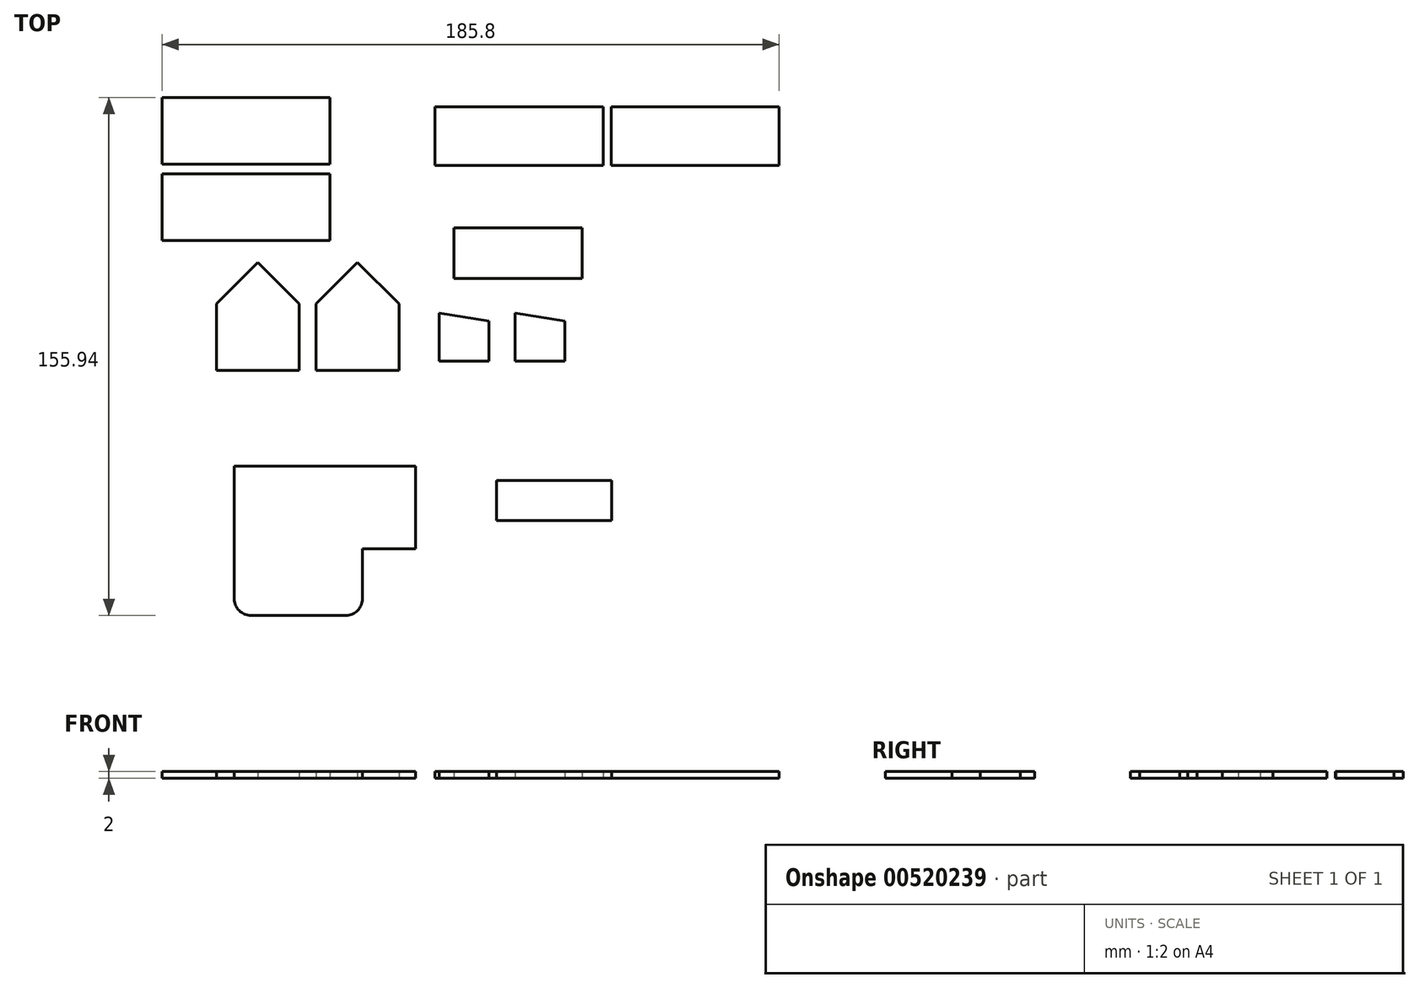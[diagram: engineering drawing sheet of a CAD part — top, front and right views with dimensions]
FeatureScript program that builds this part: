
annotation { "Feature Type Name" : "Feature", "Feature Type Description" : "" }
export const myFeature = defineFeature(function(context is Context, id is Id, definition is map)
    precondition{}
    {
        {
            var Q0;
            Q0=qCreatedBy(makeId("Top.planeOp"),FACE);
            var sketch = newSketch(context, id + "F0", { "sketchPlane" : qUnion([Q0])});
            skLineSegment(sketch, "E0.bottom", {"start": v(-52.9, 38.15) * mm, "end": v(-27.9, 38.15) * mm});
            skLineSegment(sketch, "E0.top", {"start": v(-52.9, 18.15) * mm, "end": v(-27.9, 18.15) * mm});
            skLineSegment(sketch, "E0.left", {"start": v(-52.9, 38.15) * mm, "end": v(-52.9, 18.15) * mm});
            skLineSegment(sketch, "E0.right", {"start": v(-27.9, 38.15) * mm, "end": v(-27.9, 18.15) * mm});
            skLineSegment(sketch, "E1", {"start": v(-52.9, 38.15) * mm, "end": v(-40.4, 50.65) * mm});
            skLineSegment(sketch, "E2", {"start": v(-40.4, 50.65) * mm, "end": v(-27.9, 38.15) * mm});
            skSolve(sketch);
        }
        {
            var Q0;
            Q0 = qSketchRegion(id + "F0", true);
            extrude(context, id + "F1", {"entities" : qUnion([Q0]), "depth" : 2 * mm, "offsetDistance" : 25 * mm});
        }
        {
            var Q0;
            Q0=makeQuery(id+"F1.opExtrude","SWEPT_BODY",BODY,{"disambiguationData":[OSD([sQuery(id+"F0.wireOp",EDGE,"E0.top"),sQuery(id+"F0.wireOp",EDGE,"E0.left"),sQuery(id+"F0.wireOp",EDGE,"E0.right"),sQuery(id+"F0.wireOp",EDGE,"E1"),sQuery(id+"F0.wireOp",EDGE,"E2")])]});
            transform(context, id + "F2", {"entities" : qUnion([Q0]), "transformType" : TransformType.TRANSLATION_3D, "dx" : 30 * mm, "dy" : 0 * mm, "dz" : 0 * mm, "makeCopy" : true});
        }
        {
            var Q0;
            Q0=qCreatedBy(makeId("Top.planeOp"),FACE);
            var sketch = newSketch(context, id + "F3", { "sketchPlane" : qUnion([Q0])});
            skLineSegment(sketch, "E3.bottom", {"start": v(-47.49, -10.67) * mm, "end": v(7.1, -10.67) * mm});
            skLineSegment(sketch, "E3.top", {"start": v(-47.49, -35.67) * mm, "end": v(7.1, -35.67) * mm});
            skLineSegment(sketch, "E3.left", {"start": v(-47.49, -10.67) * mm, "end": v(-47.49, -35.67) * mm});
            skLineSegment(sketch, "E3.right", {"start": v(7.1, -10.67) * mm, "end": v(7.1, -35.67) * mm});
            skLineSegment(sketch, "E4.bottom", {"start": v(-47.49, -35.67) * mm, "end": v(-8.87, -35.67) * mm});
            skLineSegment(sketch, "E4.top", {"start": v(-42.49, -55.67) * mm, "end": v(-13.87, -55.67) * mm});
            skLineSegment(sketch, "E4.left", {"start": v(-47.49, -35.67) * mm, "end": v(-47.49, -50.67) * mm});
            skLineSegment(sketch, "E4.right", {"start": v(-8.87, -35.67) * mm, "end": v(-8.87, -50.67) * mm});
            skPoint(sketch, "E5.visualSharp", {"position": v(-47.49, -55.67) * mm});
            skArc(sketch, "E5.filletArc", {"start": v(-47.49, -50.67) * mm, "mid": v(-46.02, -54.2) * mm, "end": v(-42.49, -55.67) * mm});
            skPoint(sketch, "E6.visualSharp", {"position": v(-8.87, -55.67) * mm});
            skArc(sketch, "E6.filletArc", {"start": v(-13.87, -55.67) * mm, "mid": v(-10.34, -54.2) * mm, "end": v(-8.87, -50.67) * mm});
            skSolve(sketch);
        }
        {
            var Q0;
            Q0 = qSketchRegion(id + "F3", true);
            extrude(context, id + "F4", {"entities" : qUnion([Q0]), "depth" : 2 * mm, "offsetDistance" : 25 * mm});
        }
        {
            var Q0;
            Q0=qCreatedBy(makeId("Top.planeOp"),FACE);
            var sketch = newSketch(context, id + "F5", { "sketchPlane" : qUnion([Q0])});
            skLineSegment(sketch, "E7.bottom", {"start": v(37.04, 32.92) * mm, "end": v(52.04, 32.92) * mm});
            skLineSegment(sketch, "E7.top", {"start": v(37.04, 20.92) * mm, "end": v(52.04, 20.92) * mm});
            skLineSegment(sketch, "E7.left", {"start": v(37.04, 32.92) * mm, "end": v(37.04, 20.92) * mm});
            skLineSegment(sketch, "E7.right", {"start": v(52.04, 32.92) * mm, "end": v(52.04, 20.92) * mm});
            skLineSegment(sketch, "E8", {"start": v(37.04, 32.92) * mm, "end": v(37.04, 35.42) * mm});
            skLineSegment(sketch, "E9", {"start": v(37.04, 35.42) * mm, "end": v(52.04, 32.92) * mm});
            skSolve(sketch);
        }
        {
            var Q0;
            Q0 = qSketchRegion(id + "F5", true);
            extrude(context, id + "F6", {"entities" : qUnion([Q0]), "depth" : 2 * mm, "offsetDistance" : 25 * mm});
        }
        {
            var Q0;
            Q0=makeQuery(id+"F6.opExtrude","SWEPT_BODY",BODY,{"disambiguationData":[OSD([sQuery(id+"F5.wireOp",EDGE,"E7.top"),sQuery(id+"F5.wireOp",EDGE,"E7.left"),sQuery(id+"F5.wireOp",EDGE,"E7.right"),sQuery(id+"F5.wireOp",EDGE,"E8"),sQuery(id+"F5.wireOp",EDGE,"E9")])]});
            transform(context, id + "F7", {"entities" : qUnion([Q0]), "transformType" : TransformType.TRANSLATION_3D, "dx" : -22.8 * mm, "dy" : 0 * mm, "dz" : 0 * mm, "makeCopy" : true});
        }
        {
            var Q0;
            Q0=qCreatedBy(makeId("Top.planeOp"),FACE);
            var sketch = newSketch(context, id + "F8", { "sketchPlane" : qUnion([Q0])});
            skLineSegment(sketch, "E10.bottom", {"start": v(31.5, -15.05) * mm, "end": v(66.1, -15.05) * mm});
            skLineSegment(sketch, "E10.top", {"start": v(31.5, -27.05) * mm, "end": v(66.1, -27.05) * mm});
            skLineSegment(sketch, "E10.left", {"start": v(31.5, -15.05) * mm, "end": v(31.5, -27.05) * mm});
            skLineSegment(sketch, "E10.right", {"start": v(66.1, -15.05) * mm, "end": v(66.1, -27.05) * mm});
            skSolve(sketch);
        }
        {
            var Q0;
            Q0=makeQuery(id+"F8.imprint","IMPRINT",FACE,{"disambiguationData":[TD([[makeQuery(id+"F8.imprint","IMPRINT",EDGE,{"derivedFrom":sQuery(id+"F8.wireOp",EDGE,"E10.bottom")}),-1.0]])]});
            extrude(context, id + "F9", {"entities" : qUnion([Q0]), "depth" : 2 * mm, "offsetDistance" : 25 * mm});
        }
        {
            var Q0;
            Q0=qCreatedBy(makeId("Top.planeOp"),FACE);
            var sketch = newSketch(context, id + "F10", { "sketchPlane" : qUnion([Q0])});
            skLineSegment(sketch, "E11.bottom", {"start": v(18.6, 61.06) * mm, "end": v(57.22, 61.06) * mm});
            skLineSegment(sketch, "E11.top", {"start": v(18.6, 45.85) * mm, "end": v(57.22, 45.85) * mm});
            skLineSegment(sketch, "E11.left", {"start": v(18.6, 61.06) * mm, "end": v(18.6, 45.85) * mm});
            skLineSegment(sketch, "E11.right", {"start": v(57.22, 61.06) * mm, "end": v(57.22, 45.85) * mm});
            skSolve(sketch);
        }
        {
            var Q0;
            Q0 = qSketchRegion(id + "F10", true);
            extrude(context, id + "F11", {"entities" : qUnion([Q0]), "depth" : 2 * mm, "offsetDistance" : 25 * mm});
        }
        {
            var Q0;
            Q0=qCreatedBy(makeId("Top.planeOp"),FACE);
            var sketch = newSketch(context, id + "F12", { "sketchPlane" : qUnion([Q0])});
            skLineSegment(sketch, "E12.bottom", {"start": v(-69.22, 77.27) * mm, "end": v(-18.63, 77.27) * mm});
            skLineSegment(sketch, "E12.top", {"start": v(-69.22, 57.27) * mm, "end": v(-18.63, 57.27) * mm});
            skLineSegment(sketch, "E12.left", {"start": v(-69.22, 77.27) * mm, "end": v(-69.22, 57.27) * mm});
            skLineSegment(sketch, "E12.right", {"start": v(-18.63, 77.27) * mm, "end": v(-18.63, 57.27) * mm});
            skSolve(sketch);
        }
        {
            var Q0;
            Q0 = qSketchRegion(id + "F12", true);
            extrude(context, id + "F13", {"entities" : qUnion([Q0]), "depth" : 2 * mm, "offsetDistance" : 25 * mm});
        }
        {
            var Q0;
            Q0=makeQuery(id+"F13.opExtrude","SWEPT_BODY",BODY,{"disambiguationData":[OSD([sQuery(id+"F12.wireOp",EDGE,"E12.bottom"),sQuery(id+"F12.wireOp",EDGE,"E12.top"),sQuery(id+"F12.wireOp",EDGE,"E12.left"),sQuery(id+"F12.wireOp",EDGE,"E12.right")])]});
            transform(context, id + "F14", {"entities" : qUnion([Q0]), "transformType" : TransformType.TRANSLATION_3D, "dx" : 0 * mm, "dy" : 23 * mm, "dz" : 0 * mm, "makeCopy" : true});
        }
        {
            var Q0;
            Q0=qCreatedBy(makeId("Top.planeOp"),FACE);
            var sketch = newSketch(context, id + "F15", { "sketchPlane" : qUnion([Q0])});
            skLineSegment(sketch, "E13.bottom", {"start": v(12.98, 97.47) * mm, "end": v(63.58, 97.47) * mm});
            skLineSegment(sketch, "E13.top", {"start": v(12.98, 79.8) * mm, "end": v(63.58, 79.8) * mm});
            skLineSegment(sketch, "E13.left", {"start": v(12.98, 97.47) * mm, "end": v(12.98, 79.8) * mm});
            skLineSegment(sketch, "E13.right", {"start": v(63.58, 97.47) * mm, "end": v(63.58, 79.8) * mm});
            skSolve(sketch);
        }
        {
            var Q0;
            Q0 = qSketchRegion(id + "F15", true);
            extrude(context, id + "F16", {"entities" : qUnion([Q0]), "depth" : 2 * mm, "offsetDistance" : 25 * mm});
        }
        {
            var Q0;
            Q0=makeQuery(id+"F16.opExtrude","SWEPT_BODY",BODY,{"disambiguationData":[OSD([sQuery(id+"F15.wireOp",EDGE,"E13.bottom"),sQuery(id+"F15.wireOp",EDGE,"E13.top"),sQuery(id+"F15.wireOp",EDGE,"E13.left"),sQuery(id+"F15.wireOp",EDGE,"E13.right")])]});
            transform(context, id + "F17", {"entities" : qUnion([Q0]), "transformType" : TransformType.TRANSLATION_3D, "dx" : 53 * mm, "dy" : 0 * mm, "dz" : 0 * mm, "makeCopy" : true});
        }
    });
